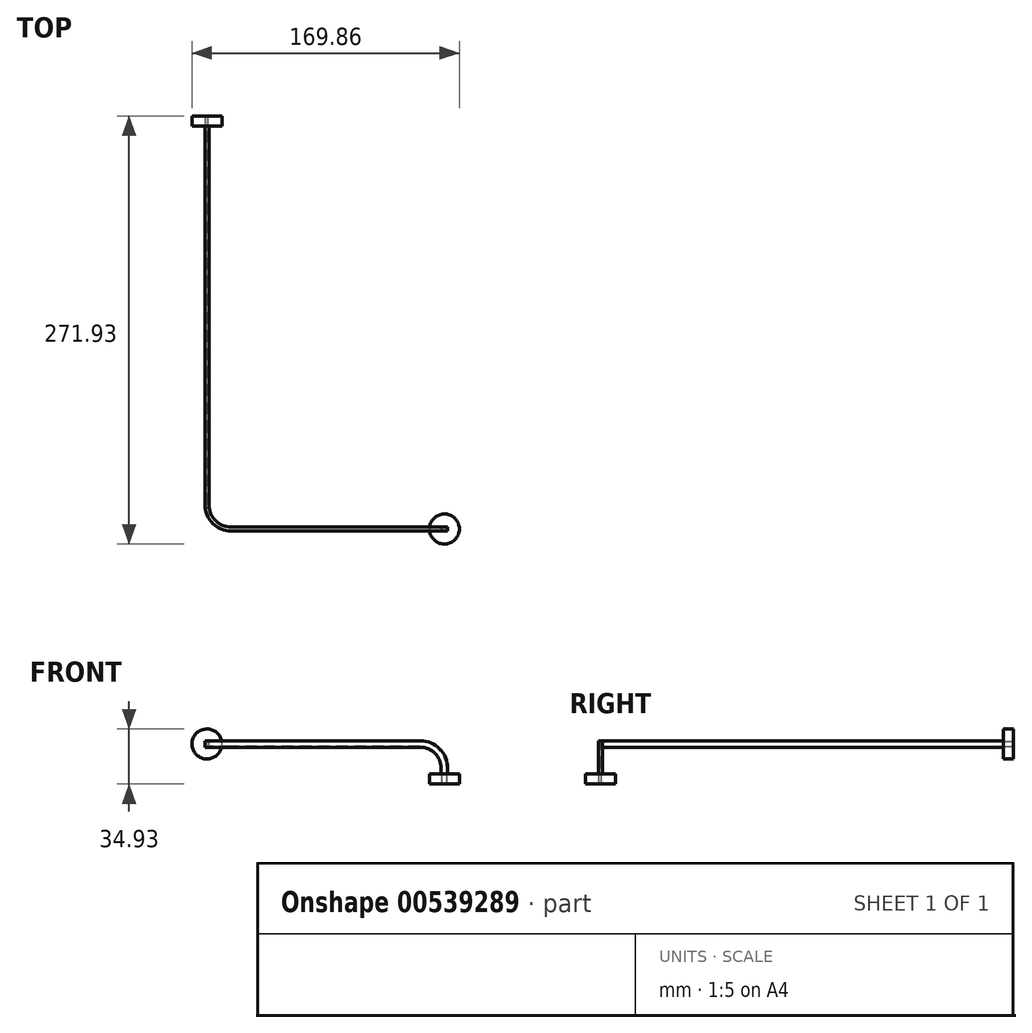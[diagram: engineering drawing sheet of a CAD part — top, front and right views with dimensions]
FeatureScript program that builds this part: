
annotation { "Feature Type Name" : "Feature", "Feature Type Description" : "" }
export const myFeature = defineFeature(function(context is Context, id is Id, definition is map)
    precondition{}
    {
        {
            var Q0;
            Q0=qCreatedBy(makeId("Front.planeOp"),FACE);
            var sketch = newSketch(context, id + "F0", { "sketchPlane" : qUnion([Q0])});
            skLineSegment(sketch, "E0.bottom", {"start": v(-0.78, -1.55) * mm, "end": v(0.77, -1.55) * mm});
            skLineSegment(sketch, "E0.top", {"start": v(-0.78, 1.55) * mm, "end": v(0.77, 1.55) * mm});
            skLineSegment(sketch, "E0.left", {"start": v(-0.78, -1.55) * mm, "end": v(-0.78, 1.55) * mm});
            skLineSegment(sketch, "E0.right", {"start": v(0.77, -1.55) * mm, "end": v(0.77, 1.55) * mm});
            skPoint(sketch, "E0.middle", {"position": v(0, 0) * mm});
            skLineSegment(sketch, "E1.bottom", {"start": v(-1.27, -2.05) * mm, "end": v(1.28, -2.05) * mm});
            skLineSegment(sketch, "E1.top", {"start": v(-1.27, 2.05) * mm, "end": v(1.28, 2.05) * mm});
            skLineSegment(sketch, "E1.left", {"start": v(-1.27, -2.05) * mm, "end": v(-1.27, 2.05) * mm});
            skLineSegment(sketch, "E1.right", {"start": v(1.28, -2.05) * mm, "end": v(1.28, 2.05) * mm});
            skCircle(sketch, "E2", {"center": v(0, 0) * mm, "radius": 9.53 * mm});
            skSolve(sketch);
        }
        {
            var Q0;
            Q0=qCreatedBy(makeId("Top.planeOp"),FACE);
            var sketch = newSketch(context, id + "F1", { "sketchPlane" : qUnion([Q0])});
            skLineSegment(sketch, "E3", {"start": v(0, 0) * mm, "end": v(0, -237) * mm});
            skLineSegment(sketch, "E4", {"start": v(0, -237) * mm, "end": v(0, -247) * mm});
            skLineSegment(sketch, "E5", {"start": v(0, -237) * mm, "end": v(25.4, -237) * mm});
            skLineSegment(sketch, "E6", {"start": v(25.4, -237) * mm, "end": v(25.4, -262.4) * mm});
            skLineSegment(sketch, "E7", {"start": v(25.4, -262.4) * mm, "end": v(15.4, -262.4) * mm});
            skArc(sketch, "E8", {"start": v(0, -247) * mm, "mid": v(4.51, -257.89) * mm, "end": v(15.4, -262.4) * mm});
            skLineSegment(sketch, "E9", {"start": v(25.4, -262.4) * mm, "end": v(125.4, -262.4) * mm});
            skSolve(sketch);
        }
        {
            var Q0;
            Q0=qCreatedBy(makeId("Front.planeOp"),FACE);
            cPlane(context, id + "F2", {"entities" : qUnion([Q0]), "cplaneType" : CPlaneType.OFFSET, "offset" : 262.4 * mm, "width" : 150 * mm, "height" : 150 * mm});
        }
        {
            var Q0;
            Q0=qCreatedBy(id+"F2.planeOp",FACE);
            var sketch = newSketch(context, id + "F3", { "sketchPlane" : qUnion([Q0])});
            skLineSegment(sketch, "E10", {"start": v(125.4, 0) * mm, "end": v(135.4, 0) * mm});
            skLineSegment(sketch, "E11", {"start": v(125.4, 0) * mm, "end": v(125.4, -25.4) * mm});
            skLineSegment(sketch, "E12", {"start": v(125.4, -25.4) * mm, "end": v(150.8, -25.4) * mm});
            skLineSegment(sketch, "E13", {"start": v(150.8, -25.4) * mm, "end": v(150.8, -15.4) * mm});
            skArc(sketch, "E14", {"start": v(150.8, -15.4) * mm, "mid": v(146.29, -4.51) * mm, "end": v(135.4, 0) * mm});
            skSolve(sketch);
        }
        {
            var Q0;
            Q0=qCreatedBy(makeId("Top.planeOp"),FACE);
            cPlane(context, id + "F4", {"entities" : qUnion([Q0]), "cplaneType" : CPlaneType.OFFSET, "offset" : 25.4 * mm, "oppositeDirection" : true, "width" : 150 * mm, "height" : 150 * mm});
        }
        {
            var Q0;
            Q0=qCreatedBy(id+"F4.planeOp",FACE);
            var sketch = newSketch(context, id + "F5", { "sketchPlane" : qUnion([Q0])});
            skLineSegment(sketch, "E15.bottom", {"start": v(152.85, -261.12) * mm, "end": v(148.75, -261.12) * mm});
            skLineSegment(sketch, "E15.top", {"start": v(152.85, -263.67) * mm, "end": v(148.75, -263.67) * mm});
            skLineSegment(sketch, "E15.left", {"start": v(152.85, -261.12) * mm, "end": v(152.85, -263.67) * mm});
            skLineSegment(sketch, "E15.right", {"start": v(148.75, -261.12) * mm, "end": v(148.75, -263.67) * mm});
            skPoint(sketch, "E15.middle", {"position": v(150.8, -262.4) * mm});
            skLineSegment(sketch, "E16.bottom", {"start": v(152.35, -261.62) * mm, "end": v(149.25, -261.62) * mm});
            skLineSegment(sketch, "E16.top", {"start": v(152.35, -263.17) * mm, "end": v(149.25, -263.17) * mm});
            skLineSegment(sketch, "E16.left", {"start": v(152.35, -261.62) * mm, "end": v(152.35, -263.17) * mm});
            skLineSegment(sketch, "E16.right", {"start": v(149.25, -261.62) * mm, "end": v(149.25, -263.17) * mm});
            skCircle(sketch, "E17", {"center": v(150.8, -262.4) * mm, "radius": 9.53 * mm});
            skSolve(sketch);
        }
        {
            var Q0;
            Q0=makeQuery(id+"F5.imprint","IMPRINT",FACE,{"disambiguationData":[TD([[makeQuery(id+"F5.imprint","IMPRINT",EDGE,{"derivedFrom":sQuery(id+"F5.wireOp",EDGE,"E15.bottom")}),1.0]])]});
            var Q1;
            Q1=sQuery(id+"F3.wireOp",EDGE,"E13");
            var Q2;
            Q2=sQuery(id+"F3.wireOp",EDGE,"E14");
            var Q3;
            Q3=sQuery(id+"F3.wireOp",EDGE,"E10");
            var Q4;
            Q4=sQuery(id+"F1.wireOp",EDGE,"E9");
            var Q5;
            Q5=sQuery(id+"F1.wireOp",EDGE,"E7");
            var Q6;
            Q6=sQuery(id+"F1.wireOp",EDGE,"E8");
            var Q7;
            Q7=sQuery(id+"F1.wireOp",EDGE,"E4");
            var Q8;
            Q8=sQuery(id+"F1.wireOp",EDGE,"E3");
            sweep(context, id + "F6", {"profiles" : qUnion([Q0]), "path" : qUnion([Q1, Q2, Q3, Q4, Q5, Q6, Q7, Q8])});
        }
        {
            var Q0;
            Q0=makeQuery(id+"F5.imprint","IMPRINT",FACE,{"disambiguationData":[TD([[makeQuery(id+"F5.imprint","IMPRINT",EDGE,{"derivedFrom":sQuery(id+"F5.wireOp",EDGE,"E15.bottom")}),-1.0]])]});
            extrude(context, id + "F7", {"entities" : qUnion([Q0]), "operationType" : NewBodyOperationType.ADD, "depth" : 6.35 * mm, "offsetDistance" : 25 * mm});
        }
        {
            var Q0;
            Q0=makeQuery(id+"F0.imprint","IMPRINT",FACE,{"disambiguationData":[TD([[makeQuery(id+"F0.imprint","IMPRINT",EDGE,{"derivedFrom":sQuery(id+"F0.wireOp",EDGE,"E1.bottom")}),-1.0]])]});
            extrude(context, id + "F8", {"entities" : qUnion([Q0]), "operationType" : NewBodyOperationType.ADD, "depth" : 6.35 * mm, "offsetDistance" : 25 * mm});
        }
    });
